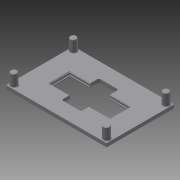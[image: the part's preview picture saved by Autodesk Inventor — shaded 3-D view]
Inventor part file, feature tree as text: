
AUTODESK INVENTOR PART (.ipt)
format: ipt  version: 2013 (Build 170138000, 138)  size: 173,056 bytes
history: native  units: mm
features: extrude x5, sketch x5, fillet x2, chamfer x1
ambient origin geometry x8: Origin, YZ Plane, XZ Plane, XY Plane, X Axis, Y Axis, Z Axis, Center Point
bodies: Solid1 (feature_tree)
feature tree (13):
  extrude  "Extrusion1"  Depth=85.5mm
  extrude  "Extrusion2"  Depth=76.5mm
  extrude  "Extrusion3"  Depth=3.5mm TaperAngle=0.0deg
  chamfer  "Chamfer1"  Distance=3.5mm
  extrude  "Extrusion4"  Depth=8.0mm
  fillet  "Fillet1"  Radius=5.0mm
  extrude  "Extrusion5"  Depth=15.0mm TaperAngle=0.0deg
  fillet  "Fillet2"  Radius=1.0mm
  sketch  "Sketch1"  dims[d0=127.7mm d1=85.5mm]
  sketch  "Sketch2"  dims[d2=4.5mm d3=0.0mm d4=76.5mm]
  sketch  "Sketch3"  dims[d5=25.5mm d6=3.5mm d7=0.0mm]
  sketch  "Sketch4"  dims[d8=1.0mm d10=3.5mm d11=0.0mm]
  sketch  "Sketch5"  dims[d12=1.0mm d13=2.0mm d14=45.0deg d15=8.0mm d17=5.0mm d18=15.0mm d19=0.0mm d20=1.0mm d22=10.0mm d24=25.0mm d25=0.0mm d26=0.0mm d27=2.0mm]
